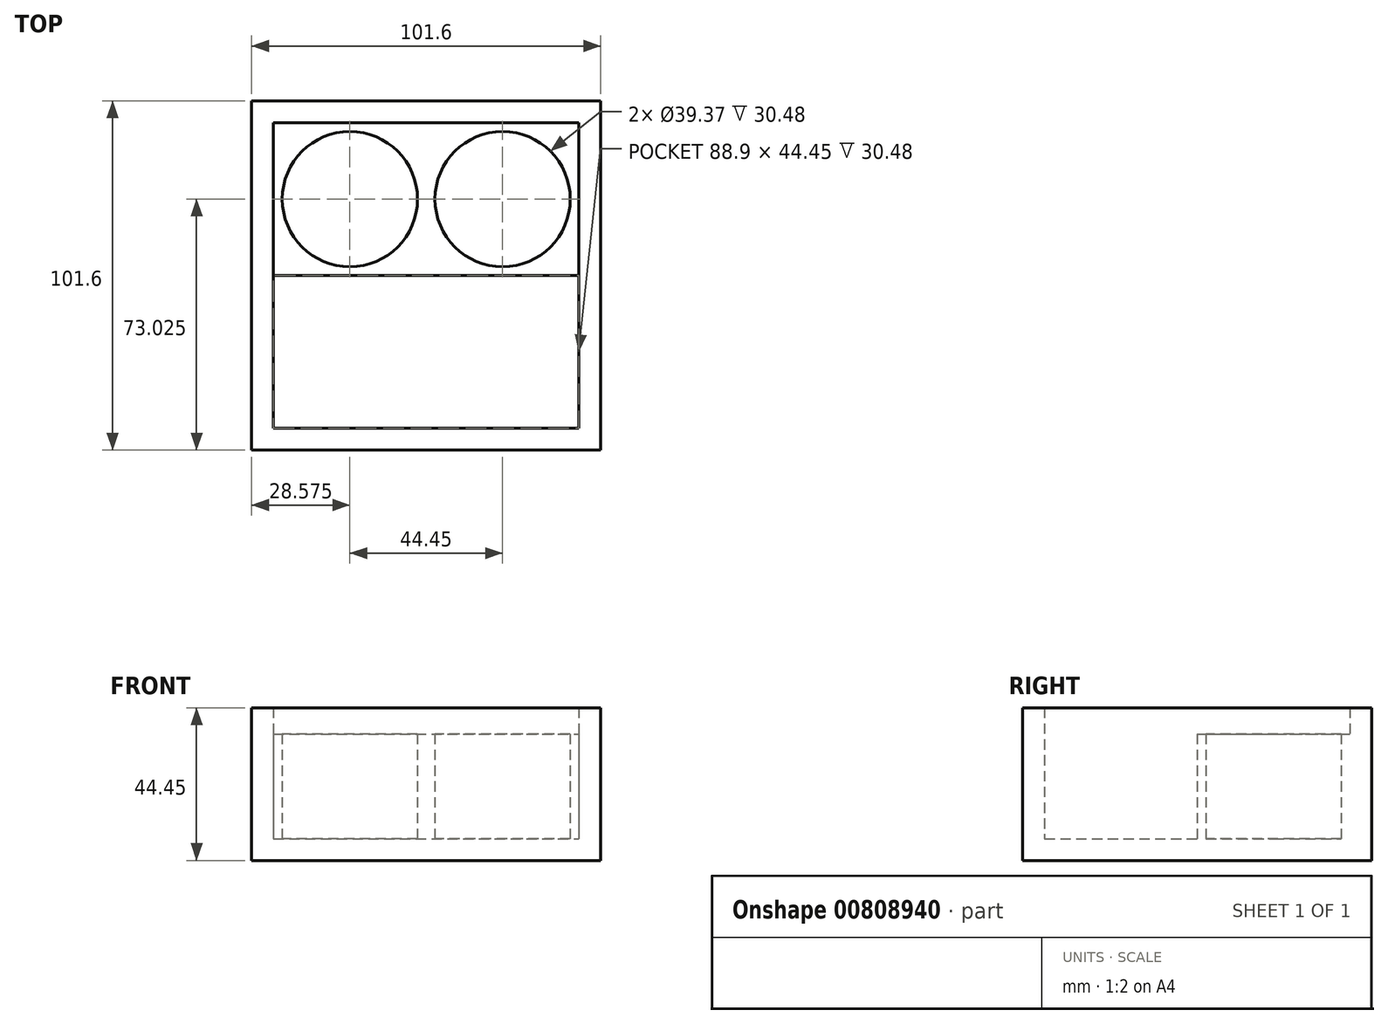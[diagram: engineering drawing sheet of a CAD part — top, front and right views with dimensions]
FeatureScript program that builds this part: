
annotation { "Feature Type Name" : "Feature", "Feature Type Description" : "" }
export const myFeature = defineFeature(function(context is Context, id is Id, definition is map)
    precondition{}
    {
        {
            var Q0;
            Q0=qCreatedBy(makeId("Top.planeOp"),FACE);
            var sketch = newSketch(context, id + "F0", { "sketchPlane" : qUnion([Q0])});
            skLineSegment(sketch, "E0.bottom", {"start": v(50.8, 50.8) * mm, "end": v(-50.8, 50.8) * mm});
            skLineSegment(sketch, "E0.top", {"start": v(50.8, -50.8) * mm, "end": v(-50.8, -50.8) * mm});
            skLineSegment(sketch, "E0.left", {"start": v(50.8, 50.8) * mm, "end": v(50.8, -50.8) * mm});
            skLineSegment(sketch, "E0.right", {"start": v(-50.8, 50.8) * mm, "end": v(-50.8, -50.8) * mm});
            skPoint(sketch, "E0.middle", {"position": v(0, 0) * mm});
            skSolve(sketch);
        }
        {
            var Q0;
            Q0=makeQuery(id+"F0.imprint","IMPRINT",FACE,{"disambiguationData":[TD([[makeQuery(id+"F0.imprint","IMPRINT",EDGE,{"derivedFrom":sQuery(id+"F0.wireOp",EDGE,"E0.bottom")}),1.0]])]});
            extrude(context, id + "F1", {"entities" : qUnion([Q0]), "depth" : 6.35 * mm, "offsetDistance" : 25.4 * mm});
        }
        {
            var Q0;
            Q0=makeQuery(id+"F1.opExtrude","CAP_FACE",FACE,{"disambiguationData":[OSD([sQuery(id+"F0.wireOp",EDGE,"E0.bottom"),sQuery(id+"F0.wireOp",EDGE,"E0.top"),sQuery(id+"F0.wireOp",EDGE,"E0.left"),sQuery(id+"F0.wireOp",EDGE,"E0.right")])],"isStart":false});
            var sketch = newSketch(context, id + "F2", { "sketchPlane" : qUnion([Q0])});
            skLineSegment(sketch, "E1.bottom", {"start": v(-50.8, 50.8) * mm, "end": v(50.8, 50.8) * mm});
            skLineSegment(sketch, "E1.top", {"start": v(-50.8, 44.45) * mm, "end": v(50.8, 44.45) * mm});
            skLineSegment(sketch, "E1.left", {"start": v(-50.8, 50.8) * mm, "end": v(-50.8, 44.45) * mm});
            skLineSegment(sketch, "E1.right", {"start": v(50.8, 50.8) * mm, "end": v(50.8, 44.45) * mm});
            skLineSegment(sketch, "E2.bottom", {"start": v(50.8, 44.45) * mm, "end": v(44.45, 44.45) * mm});
            skLineSegment(sketch, "E2.top", {"start": v(50.8, -50.8) * mm, "end": v(44.45, -50.8) * mm});
            skLineSegment(sketch, "E2.left", {"start": v(50.8, 44.45) * mm, "end": v(50.8, -50.8) * mm});
            skLineSegment(sketch, "E2.right", {"start": v(44.45, 44.45) * mm, "end": v(44.45, -50.8) * mm});
            skLineSegment(sketch, "E3.bottom", {"start": v(44.45, -50.8) * mm, "end": v(-50.8, -50.8) * mm});
            skLineSegment(sketch, "E3.top", {"start": v(44.45, -44.45) * mm, "end": v(-50.8, -44.45) * mm});
            skLineSegment(sketch, "E3.left", {"start": v(44.45, -50.8) * mm, "end": v(44.45, -44.45) * mm});
            skLineSegment(sketch, "E3.right", {"start": v(-50.8, -50.8) * mm, "end": v(-50.8, -44.45) * mm});
            skLineSegment(sketch, "E4.bottom", {"start": v(-50.8, -44.45) * mm, "end": v(-44.45, -44.45) * mm});
            skLineSegment(sketch, "E4.top", {"start": v(-50.8, 44.45) * mm, "end": v(-44.45, 44.45) * mm});
            skLineSegment(sketch, "E4.left", {"start": v(-50.8, -44.45) * mm, "end": v(-50.8, 44.45) * mm});
            skLineSegment(sketch, "E4.right", {"start": v(-44.45, -44.45) * mm, "end": v(-44.45, 44.45) * mm});
            skSolve(sketch);
        }
        {
            var Q0;
            Q0=qSketchRegion(id+"F2",true);
            extrude(context, id + "F3", {"entities" : qUnion([Q0]), "operationType" : NewBodyOperationType.ADD, "depth" : 38.1 * mm, "offsetDistance" : 25.4 * mm});
        }
        {
            var Q0;
            Q0=makeQuery(id+"F1.opExtrude","CAP_FACE",FACE,{"disambiguationData":[OSD([sQuery(id+"F0.wireOp",EDGE,"E0.bottom"),sQuery(id+"F0.wireOp",EDGE,"E0.top"),sQuery(id+"F0.wireOp",EDGE,"E0.left"),sQuery(id+"F0.wireOp",EDGE,"E0.right")])],"isStart":false});
            var sketch = newSketch(context, id + "F4", { "sketchPlane" : qUnion([Q0])});
            skLineSegment(sketch, "E5", {"start": v(0, 44.45) * mm, "end": v(0, -44.45) * mm});
            skLineSegment(sketch, "E6", {"start": v(-44.45, 0) * mm, "end": v(44.45, 0) * mm});
            skLineSegment(sketch, "E7", {"start": v(0, 0) * mm, "end": v(-44.45, 0) * mm});
            skLineSegment(sketch, "E8", {"start": v(0, 0) * mm, "end": v(44.45, 0) * mm});
            skLineSegment(sketch, "E9", {"start": v(0, 0) * mm, "end": v(0, 44.45) * mm});
            skLineSegment(sketch, "E10", {"start": v(0, 0) * mm, "end": v(0, -44.45) * mm});
            skLineSegment(sketch, "E11.bottom", {"start": v(-44.45, 44.45) * mm, "end": v(0, 44.45) * mm});
            skLineSegment(sketch, "E11.top", {"start": v(-44.45, 0) * mm, "end": v(0, 0) * mm});
            skLineSegment(sketch, "E11.left", {"start": v(-44.45, 44.45) * mm, "end": v(-44.45, 0) * mm});
            skLineSegment(sketch, "E11.right", {"start": v(0, 44.45) * mm, "end": v(0, 0) * mm});
            skLineSegment(sketch, "E12.top", {"start": v(0, 44.45) * mm, "end": v(44.45, 44.45) * mm});
            skLineSegment(sketch, "E12.right", {"start": v(44.45, 0) * mm, "end": v(44.45, 44.45) * mm});
            skLineSegment(sketch, "E13.top", {"start": v(0, -44.45) * mm, "end": v(44.45, -44.45) * mm});
            skLineSegment(sketch, "E13.right", {"start": v(44.45, 0) * mm, "end": v(44.45, -44.45) * mm});
            skLineSegment(sketch, "E14.top", {"start": v(0, -44.45) * mm, "end": v(-44.45, -44.45) * mm});
            skLineSegment(sketch, "E14.right", {"start": v(-44.45, 0) * mm, "end": v(-44.45, -44.45) * mm});
            skCircle(sketch, "E15", {"center": v(-22.23, -22.23) * mm, "radius": 19.69 * mm});
            skPoint(sketch, "E15.centerSnap0", {"position": v(0, -22.23) * mm});
            skPoint(sketch, "E15.centerSnap1", {"position": v(-22.23, 0) * mm});
            skCircle(sketch, "E16", {"center": v(-22.23, 22.23) * mm, "radius": 19.69 * mm});
            skPoint(sketch, "E16.centerSnap0", {"position": v(0, 22.22) * mm});
            skCircle(sketch, "E17", {"center": v(22.23, 22.23) * mm, "radius": 19.69 * mm});
            skPoint(sketch, "E17.centerSnap0", {"position": v(22.23, 0) * mm});
            skCircle(sketch, "E18", {"center": v(22.23, -22.23) * mm, "radius": 19.69 * mm});
            skSolve(sketch);
        }
        {
            var Q0;
            Q0=makeQuery(id+"F4.imprint","IMPRINT",FACE,{"disambiguationData":[TD([[makeQuery(id+"F4.imprint","IMPRINT",EDGE,{"derivedFrom":sQuery(id+"F4.wireOp",EDGE,"E11.bottom")}),-1.0]])]});
            var Q1;
            Q1=makeQuery(id+"F4.imprint","IMPRINT",FACE,{"disambiguationData":[TD([[makeQuery(id+"F4.imprint","IMPRINT",EDGE,{"derivedFrom":sQuery(id+"F4.wireOp",EDGE,"E12.top")}),-1.0]])]});
            var Q2;
            Q2=makeQuery(id+"F4.imprint","IMPRINT",FACE,{"disambiguationData":[TD([[makeQuery(id+"F4.imprint","IMPRINT",EDGE,{"derivedFrom":sQuery(id+"F4.wireOp",EDGE,"E8")}),-1.0]])]});
            var Q3;
            Q3=makeQuery(id+"F4.imprint","IMPRINT",FACE,{"disambiguationData":[TD([[makeQuery(id+"F4.imprint","IMPRINT",EDGE,{"derivedFrom":sQuery(id+"F4.wireOp",EDGE,"E7")}),1.0]])]});
            extrude(context, id + "F5", {"entities" : qUnion([Q0, Q1, Q2, Q3]), "operationType" : NewBodyOperationType.ADD, "depth" : 30.48 * mm, "offsetDistance" : 25.4 * mm});
        }
    });
